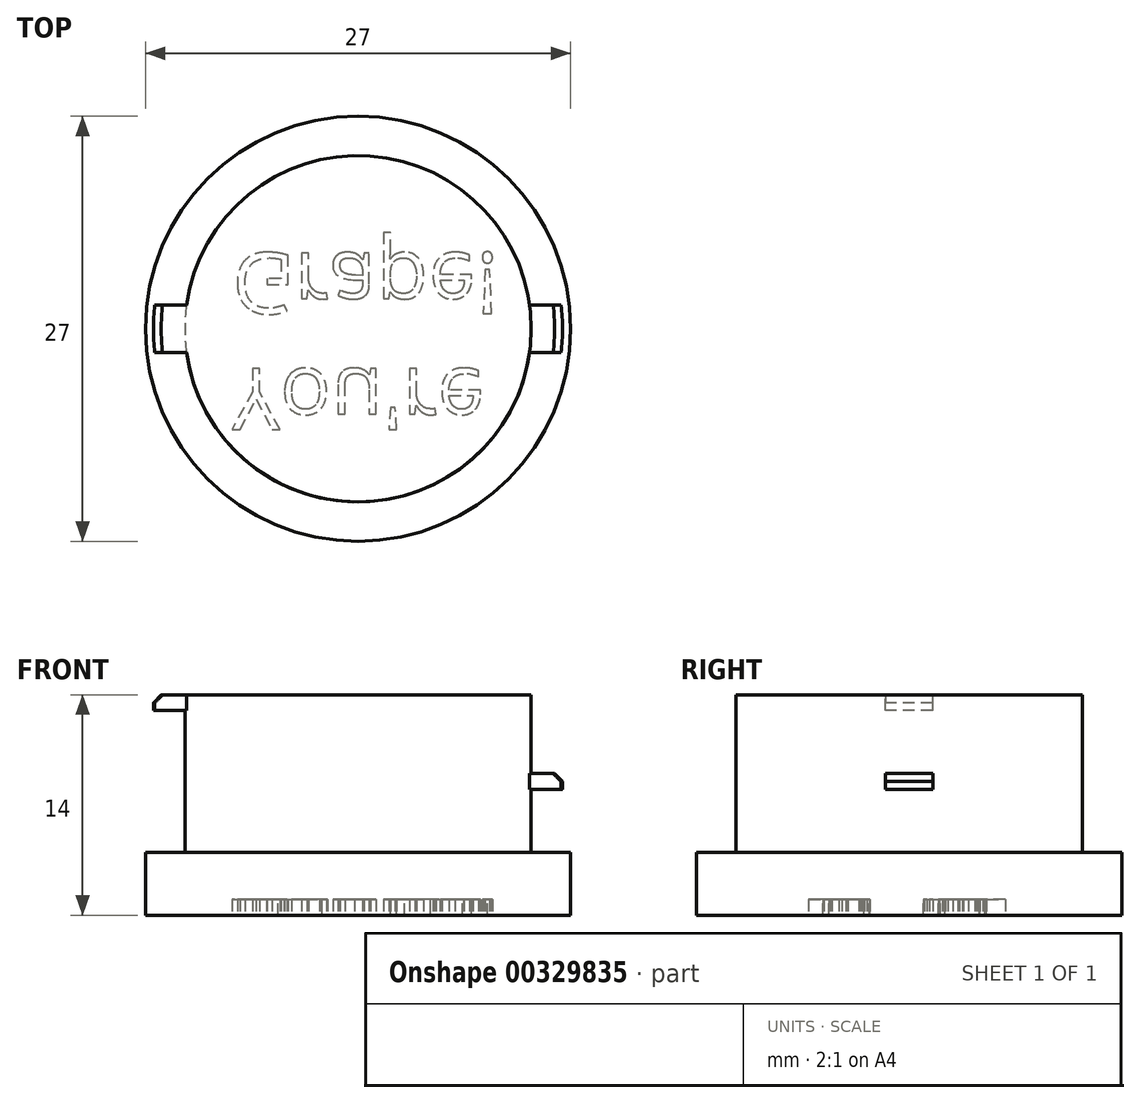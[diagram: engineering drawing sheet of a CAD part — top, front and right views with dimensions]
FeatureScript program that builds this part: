
annotation { "Feature Type Name" : "Feature", "Feature Type Description" : "" }
export const myFeature = defineFeature(function(context is Context, id is Id, definition is map)
    precondition{}
    {
        {
            var Q0;
            Q0=qCreatedBy(makeId("Top.planeOp"),FACE);
            var sketch = newSketch(context, id + "F0", { "sketchPlane" : qUnion([Q0])});
            skCircle(sketch, "E0", {"center": v(0, 0) * mm, "radius": 13.5 * mm});
            skSolve(sketch);
        }
        {
            var Q0;
            Q0 = qSketchRegion(id + "F0", true);
            extrude(context, id + "F1", {"entities" : qUnion([Q0]), "depth" : 4 * mm, "offsetDistance" : 25 * mm});
        }
        {
            var Q0;
            Q0=makeQuery(id+"F1.opExtrude","CAP_FACE",FACE,{"disambiguationData":[OSD([sQuery(id+"F0.wireOp",EDGE,"E0")])],"isStart":false});
            var sketch = newSketch(context, id + "F2", { "sketchPlane" : qUnion([Q0])});
            skCircle(sketch, "E1", {"center": v(0, 0) * mm, "radius": 11 * mm});
            skSolve(sketch);
        }
        {
            var Q0;
            Q0 = qSketchRegion(id + "F2", true);
            extrude(context, id + "F3", {"entities" : qUnion([Q0]), "operationType" : NewBodyOperationType.ADD, "depth" : 10 * mm, "offsetDistance" : 25 * mm});
        }
        {
            var Q0;
            Q0=makeQuery(id+"F3.opExtrude","CAP_FACE",FACE,{"disambiguationData":[OSD([sQuery(id+"F2.wireOp",EDGE,"E1")])],"isStart":false});
            var sketch = newSketch(context, id + "F4", { "sketchPlane" : qUnion([Q0])});
            skArc(sketch, "E2", {"start": v(-12.91, 1.5) * mm, "mid": v(-13, 0) * mm, "end": v(-12.91, -1.5) * mm});
            skLineSegment(sketch, "E3", {"start": v(-13, 0) * mm, "end": v(-11, 0) * mm, "construction": true});
            skArc(sketch, "E4", {"start": v(-10.9, 1.5) * mm, "mid": v(-11, 0) * mm, "end": v(-10.9, -1.5) * mm});
            skLineSegment(sketch, "E5", {"start": v(-12.91, 1.5) * mm, "end": v(-10.9, 1.5) * mm});
            skLineSegment(sketch, "E6", {"start": v(-12.91, -1.5) * mm, "end": v(-10.9, -1.5) * mm});
            skSolve(sketch);
        }
        {
            var Q0;
            Q0 = qSketchRegion(id + "F4", true);
            extrude(context, id + "F5", {"entities" : qUnion([Q0]), "operationType" : NewBodyOperationType.ADD, "oppositeDirection" : true, "depth" : 1 * mm, "offsetDistance" : 25 * mm});
        }
        {
            var Q0;
            Q0=makeQuery(id+"F1.opExtrude","CAP_FACE",FACE,{"disambiguationData":[OSD([sQuery(id+"F0.wireOp",EDGE,"E0")])],"isStart":false});
            cPlane(context, id + "F6", {"entities" : qUnion([Q0]), "cplaneType" : CPlaneType.OFFSET, "offset" : 4 * mm, "width" : 150 * mm, "height" : 150 * mm});
        }
        {
            var Q0;
            Q0=qCreatedBy(id+"F6.planeOp",FACE);
            var sketch = newSketch(context, id + "F7", { "sketchPlane" : qUnion([Q0])});
            skArc(sketch, "E7", {"start": v(12.9, -1.5) * mm, "mid": v(12.98, 0) * mm, "end": v(12.9, 1.5) * mm});
            skArc(sketch, "E8", {"start": v(10.9, -1.5) * mm, "mid": v(11, 0) * mm, "end": v(10.9, 1.5) * mm});
            skLineSegment(sketch, "E9", {"start": v(10.9, 1.5) * mm, "end": v(12.9, 1.5) * mm});
            skLineSegment(sketch, "E10", {"start": v(10.9, -1.5) * mm, "end": v(12.9, -1.5) * mm});
            skLineSegment(sketch, "E11", {"start": v(11, 0) * mm, "end": v(12.98, 0) * mm, "construction": true});
            skSolve(sketch);
        }
        {
            var Q0;
            Q0 = qSketchRegion(id + "F7", true);
            extrude(context, id + "F8", {"entities" : qUnion([Q0]), "operationType" : NewBodyOperationType.ADD, "depth" : 1 * mm, "offsetDistance" : 25 * mm});
        }
        {
            var Q0;
            Q0=makeQuery(id+"F5.opExtrude","CAP_EDGE",EDGE,{"disambiguationData":[OSD([sQuery(id+"F4.wireOp",EDGE,"E2")])],"isStart":true});
            var Q1;
            Q1=makeQuery(id+"F8.opExtrude","CAP_EDGE",EDGE,{"disambiguationData":[OSD([sQuery(id+"F7.wireOp",EDGE,"E7")])],"isStart":false});
            chamfer(context, id + "F9", {"entities" : qUnion([Q0, Q1]), "width" : .5 * mm, "tangentPropagation" : true});
        }
        {
            var Q0;
            Q0=makeQuery(id+"F1.opExtrude","CAP_FACE",FACE,{"disambiguationData":[OSD([sQuery(id+"F0.wireOp",EDGE,"E0")])],"isStart":true});
            var sketch = newSketch(context, id + "F10", { "sketchPlane" : qUnion([Q0])});
            skText(sketch, "E12", { "text": "You\'re\nGrape!", "fontName": "OpenSans-Regular.ttf"});
            const initialGuessF10  = {"E12": [-0.00799, 0.00253, 1, 0, 0.00389]};
            skSetInitialGuess(sketch, initialGuessF10);
            skSolve(sketch);
        }
        {
            var Q0;
            Q0 = qSketchRegion(id + "F10", true);
            extrude(context, id + "F11", {"entities" : qUnion([Q0]), "operationType" : NewBodyOperationType.REMOVE, "oppositeDirection" : true, "depth" : 1 * mm, "offsetDistance" : 25 * mm});
        }
    });
